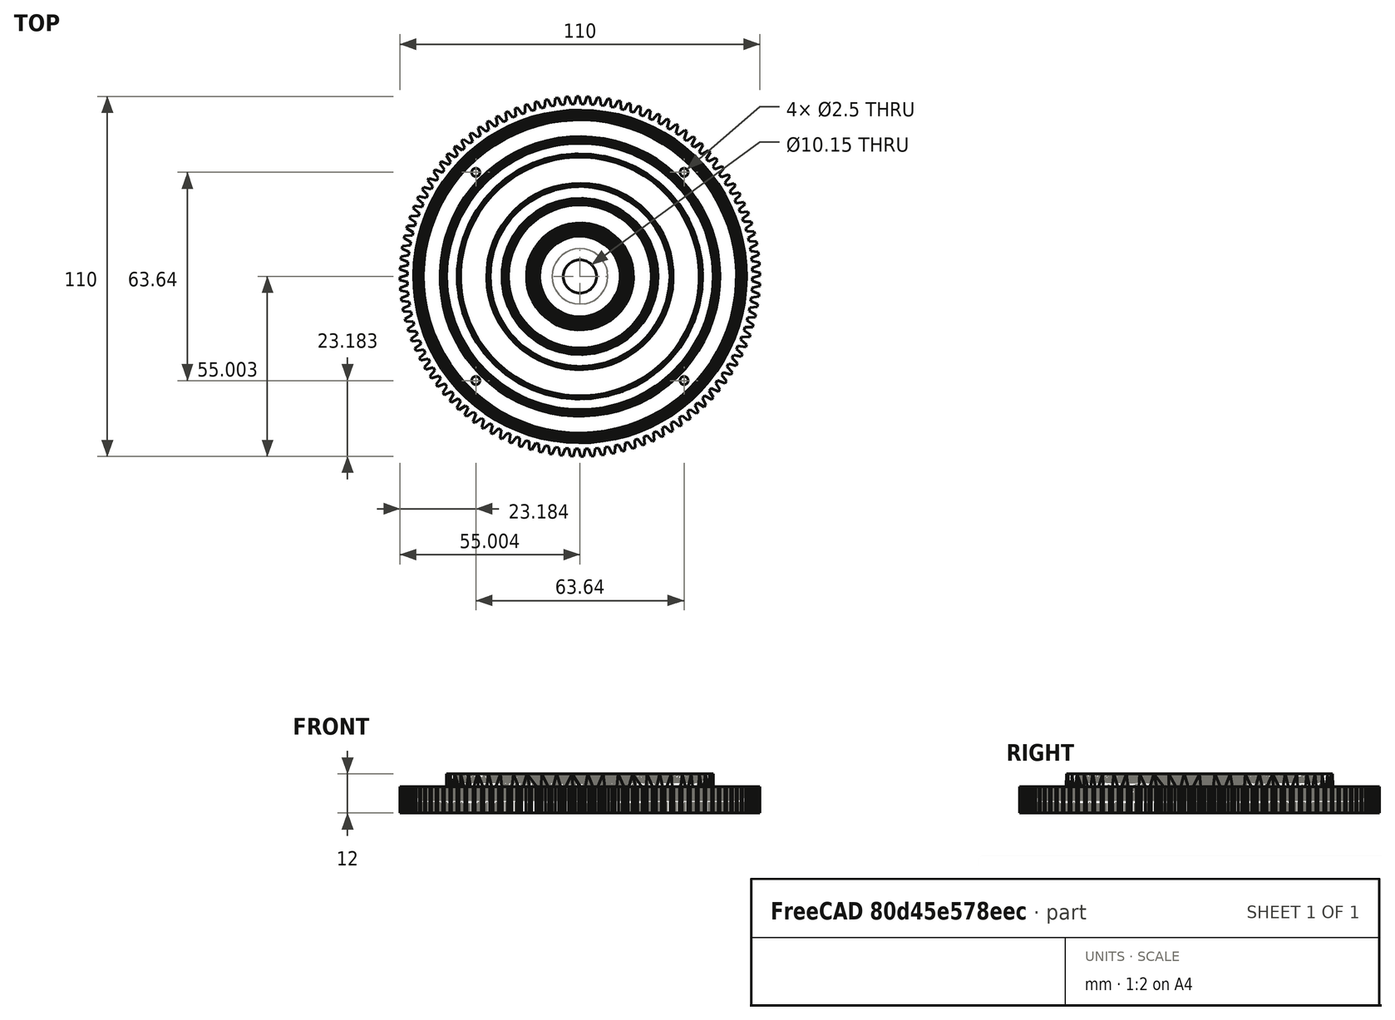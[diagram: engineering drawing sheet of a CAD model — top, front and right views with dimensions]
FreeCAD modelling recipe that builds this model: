
FCSTD DOCUMENT  (FreeCAD 0.21R33668 +26 (Git))
Label: Robot_Base_Low_Gear
License: All rights reserved
LicenseURL: https://en.wikipedia.org/wiki/All_rights_reserved
objects: Part::Feature×1, PartDesign::FeatureBase×1, Sketcher::SketchObject×1, PartDesign::Pocket×1, PartDesign::Body×1
note: 6 computed .brp shape members not serialized (recipe doc carries the construction recipe); baked Part::Feature solids carry a one-line shape summary decoded from their .brp

FEATURE [Part::Feature] Part__Feature  label="Robot_Base_Low_Gear"
  shape: bbox 110 x 110 x 12 mm, 11468 faces (baked)
FEATURE [PartDesign::FeatureBase] BaseFeature
  BaseFeature = -> Part__Feature
FEATURE [Sketcher::SketchObject] Sketch
  ExternalGeometry = -> [BaseFeature]
  FullyConstrained = false
  MapMode = 5
  Placement = pos=(0,0,79.9933) rot=(0,0,1;0rad)
  Support = -> [BaseFeature]
  sketch-geometry (6):
    g0: Circle CenterX=82.4042 CenterY=86.933 CenterZ=0 NormalX=0 NormalY=0 NormalZ=1 AngleXU=0 Radius=5.075
    g1: GeomPoint X=82.4042 Y=86.933 Z=0
    g2: Circle CenterX=114.224 CenterY=118.753 CenterZ=0 NormalX=0 NormalY=0 NormalZ=1 AngleXU=0 Radius=1.25
    g3: Circle CenterX=114.224 CenterY=55.1132 CenterZ=0 NormalX=0 NormalY=0 NormalZ=1 AngleXU=0 Radius=1.25
    g4: Circle CenterX=50.5844 CenterY=55.1132 CenterZ=0 NormalX=0 NormalY=0 NormalZ=1 AngleXU=0 Radius=1.25
    g5: Circle CenterX=50.5844 CenterY=118.753 CenterZ=0 NormalX=0 NormalY=0 NormalZ=1 AngleXU=0 Radius=1.25
  constraints (5):
    c: Diameter(g0) = 10.15
    c: Diameter(g2) = 2.5
    c: Diameter(g5) = 2.5
    c: Diameter(g4) = 2.5
    c: Diameter(g3) = 2.5
FEATURE [PartDesign::Pocket] Pocket
  BaseFeature = -> BaseFeature
  Direction = (0,0,-1)
  Length = 5
  Length2 = 5
  Profile = -> Sketch
  ReferenceAxis = -> Sketch [N_Axis]
  Type = 1
FEATURE [PartDesign::Body] Body
  BaseFeature = -> Part__Feature
  Group = -> [BaseFeature,Sketch,Pocket]
  Origin = -> Origin
  Tip = -> Pocket
